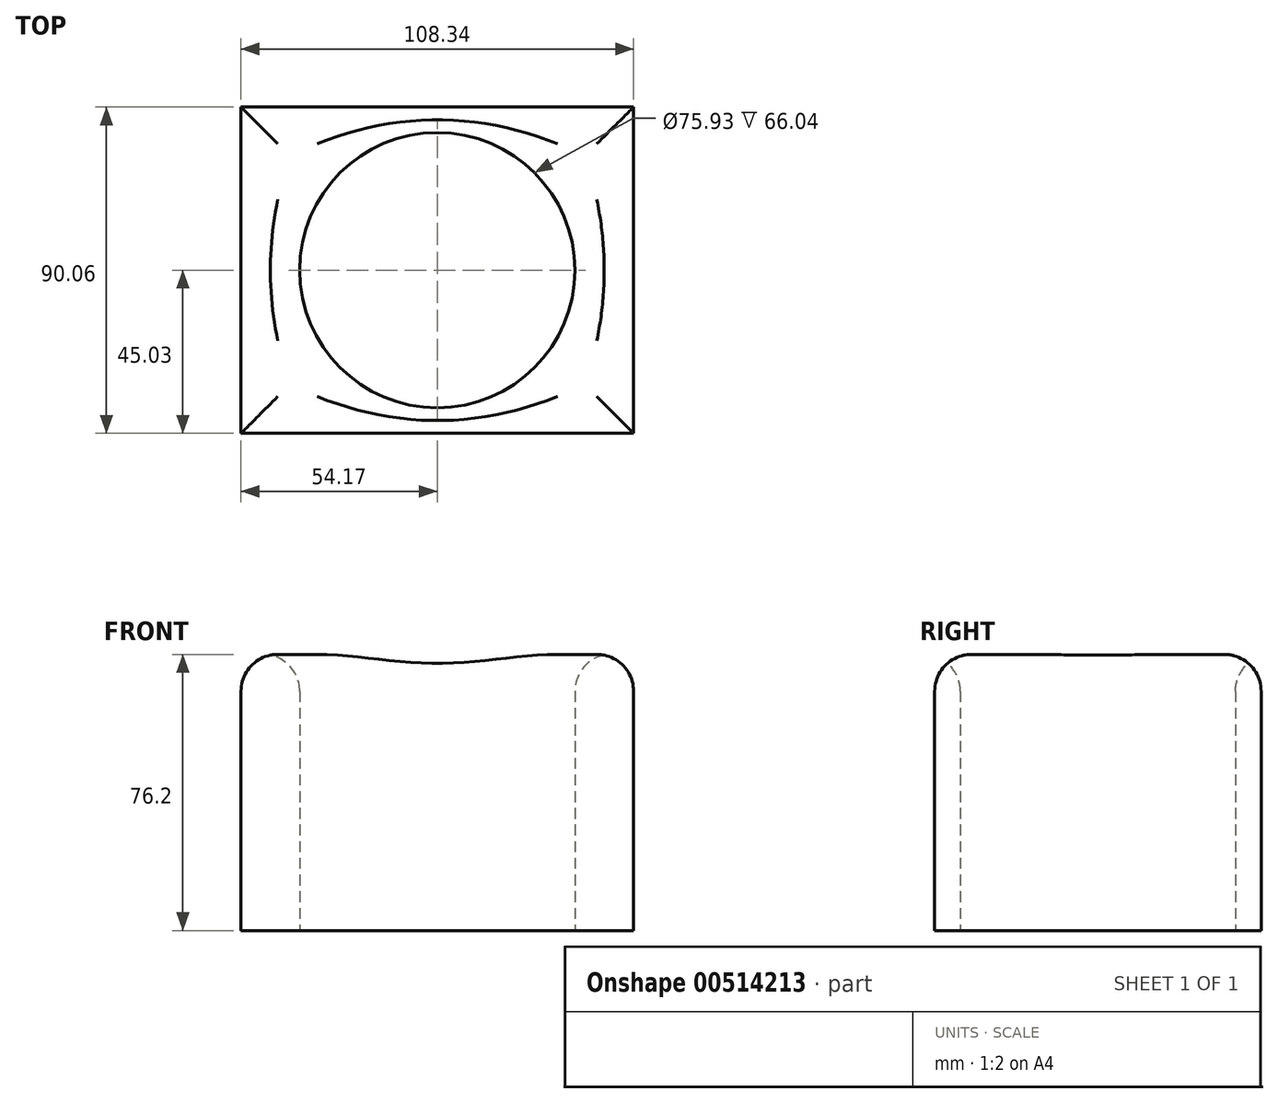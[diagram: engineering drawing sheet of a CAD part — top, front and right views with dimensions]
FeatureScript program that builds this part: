
annotation { "Feature Type Name" : "Feature", "Feature Type Description" : "" }
export const myFeature = defineFeature(function(context is Context, id is Id, definition is map)
    precondition{}
    {
        {
            var Q0;
            Q0=qCreatedBy(makeId("Top.planeOp"),FACE);
            var sketch = newSketch(context, id + "F0", { "sketchPlane" : qUnion([Q0])});
            skCircle(sketch, "E0", {"center": v(0, 0) * mm, "radius": 37.97 * mm});
            skLineSegment(sketch, "E1.bottom", {"start": v(54.17, -45.03) * mm, "end": v(-54.17, -45.03) * mm});
            skLineSegment(sketch, "E1.top", {"start": v(54.17, 45.03) * mm, "end": v(-54.17, 45.03) * mm});
            skLineSegment(sketch, "E1.left", {"start": v(54.17, -45.03) * mm, "end": v(54.17, 45.03) * mm});
            skLineSegment(sketch, "E1.right", {"start": v(-54.17, -45.03) * mm, "end": v(-54.17, 45.03) * mm});
            skSolve(sketch);
        }
        {
            var Q0;
            Q0 = qSketchRegion(id + "F0", true);
            extrude(context, id + "F1", {"entities" : qUnion([Q0]), "depth" : 76.2 * mm});
        }
        {
            var Q0;
            Q0=makeQuery(id+"F1.opExtrude","CAP_EDGE",EDGE,{"disambiguationData":[OSD([sQuery(id+"F0.wireOp",EDGE,"E1.bottom")])],"isStart":false});
            var Q1;
            Q1=makeQuery(id+"F1.opExtrude","CAP_EDGE",EDGE,{"disambiguationData":[OSD([sQuery(id+"F0.wireOp",EDGE,"E1.right")])],"isStart":false});
            var Q2;
            Q2=makeQuery(id+"F1.opExtrude","CAP_FACE",FACE,{"disambiguationData":[OSD([sQuery(id+"F0.wireOp",EDGE,"E0"),sQuery(id+"F0.wireOp",EDGE,"E1.bottom"),sQuery(id+"F0.wireOp",EDGE,"E1.top"),sQuery(id+"F0.wireOp",EDGE,"E1.left"),sQuery(id+"F0.wireOp",EDGE,"E1.right")])],"isStart":false});
            var Q3;
            Q3=makeQuery(id+"F1.opExtrude","CAP_EDGE",EDGE,{"disambiguationData":[OSD([sQuery(id+"F0.wireOp",EDGE,"E1.top")])],"isStart":false});
            fillet(context, id + "F2", {"entities" : qUnion([Q0, Q1, Q2, Q3]), "radius" : 10.16 * mm, "tangentPropagation" : true, "allowEdgeOverflow" : false});
        }
    });
